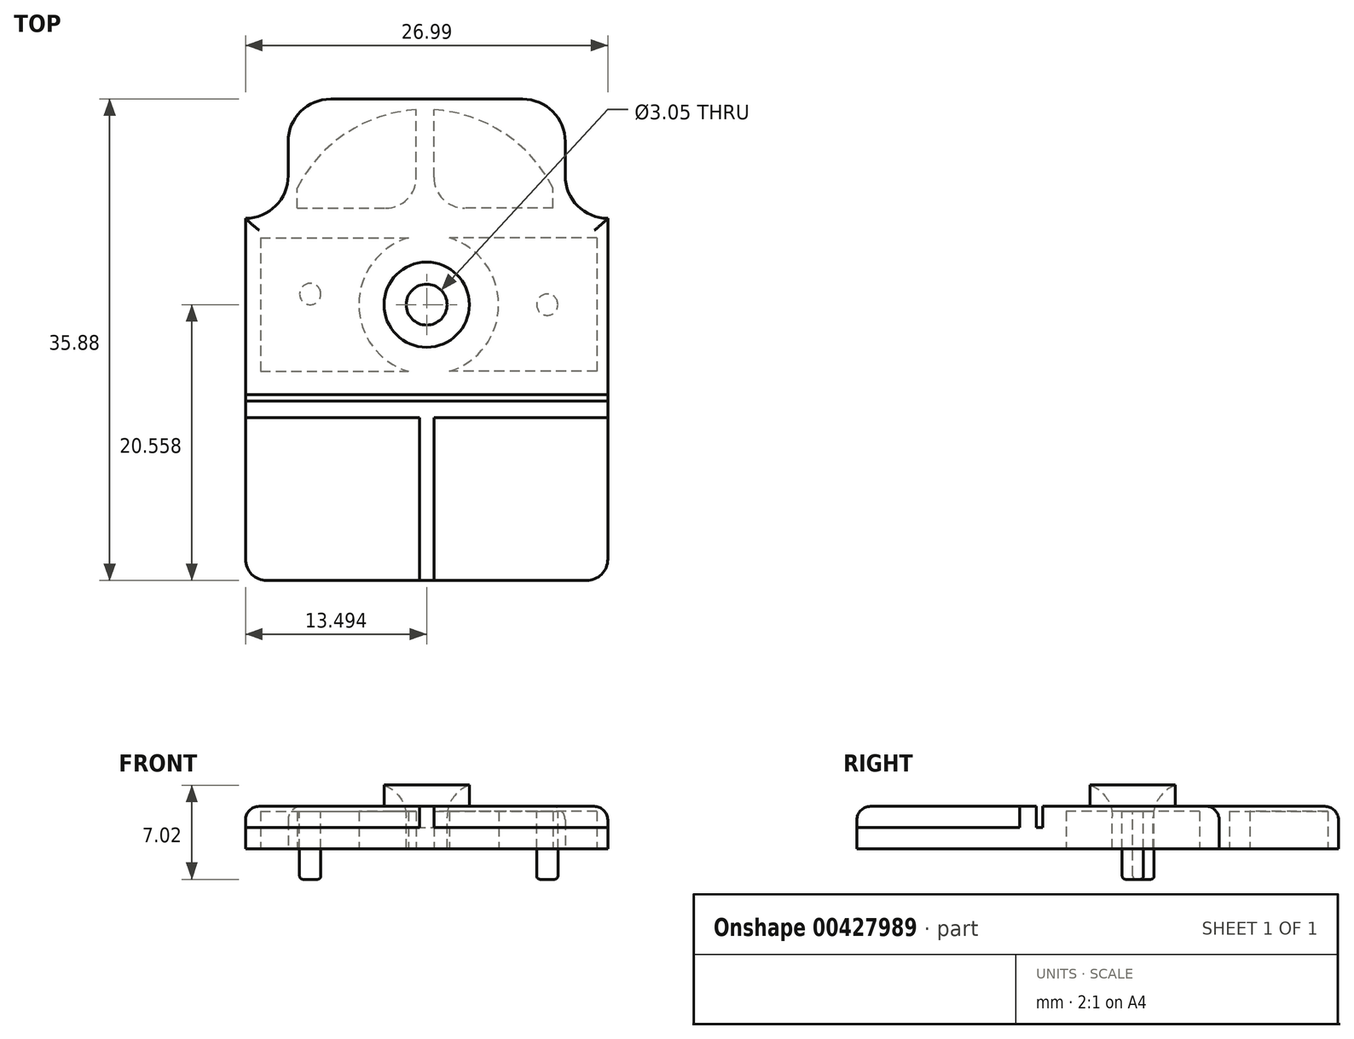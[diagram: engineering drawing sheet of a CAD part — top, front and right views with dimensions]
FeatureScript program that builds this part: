
annotation { "Feature Type Name" : "Feature", "Feature Type Description" : "" }
export const myFeature = defineFeature(function(context is Context, id is Id, definition is map)
    precondition{}
    {
        {
            var Q0;
            Q0=qCreatedBy(makeId("Top.planeOp"),FACE);
            var sketch = newSketch(context, id + "F0", { "sketchPlane" : qUnion([Q0])});
            skLineSegment(sketch, "E0", {"start": v(1.59, 0) * mm, "end": v(25.4, 0) * mm});
            skLineSegment(sketch, "E1", {"start": v(26.99, 1.59) * mm, "end": v(26.99, 26.99) * mm});
            skLineSegment(sketch, "E2", {"start": v(0, 1.59) * mm, "end": v(0, 26.99) * mm});
            skLineSegment(sketch, "E3", {"start": v(26.99, 26.99) * mm, "end": v(26.99, 26.99) * mm});
            skLineSegment(sketch, "E4", {"start": v(0, 26.99) * mm, "end": v(0, 26.99) * mm});
            skLineSegment(sketch, "E5", {"start": v(23.81, 30.16) * mm, "end": v(23.81, 32.7) * mm});
            skLineSegment(sketch, "E6", {"start": v(3.18, 30.16) * mm, "end": v(3.18, 32.7) * mm});
            skLineSegment(sketch, "E7", {"start": v(6.35, 35.88) * mm, "end": v(20.64, 35.88) * mm});
            skPoint(sketch, "E8.visualSharp", {"position": v(26.99, 0) * mm});
            skArc(sketch, "E8.filletArc", {"start": v(25.4, 0) * mm, "mid": v(26.52, 0.46) * mm, "end": v(26.99, 1.59) * mm});
            skPoint(sketch, "E9.visualSharp", {"position": v(0, 0) * mm});
            skArc(sketch, "E9.filletArc", {"start": v(0, 1.59) * mm, "mid": v(0.46, 0.46) * mm, "end": v(1.59, 0) * mm});
            skPoint(sketch, "E10.visualSharp", {"position": v(23.81, 35.88) * mm});
            skArc(sketch, "E10.filletArc", {"start": v(23.81, 32.7) * mm, "mid": v(22.88, 34.95) * mm, "end": v(20.64, 35.88) * mm});
            skPoint(sketch, "E11.visualSharp", {"position": v(3.18, 35.88) * mm});
            skArc(sketch, "E11.filletArc", {"start": v(6.35, 35.88) * mm, "mid": v(4.1, 34.95) * mm, "end": v(3.17, 32.7) * mm});
            skPoint(sketch, "E12.visualSharp", {"position": v(23.81, 26.99) * mm});
            skArc(sketch, "E12.filletArc", {"start": v(23.81, 30.16) * mm, "mid": v(24.74, 27.92) * mm, "end": v(26.99, 26.99) * mm});
            skPoint(sketch, "E13.visualSharp", {"position": v(3.18, 26.99) * mm});
            skArc(sketch, "E13.filletArc", {"start": v(0, 26.99) * mm, "mid": v(2.25, 27.92) * mm, "end": v(3.18, 30.16) * mm});
            skSolve(sketch);
        }
        {
            var Q0;
            Q0=makeQuery(id+"F0.imprint","IMPRINT",FACE,{"disambiguationData":[TD([[makeQuery(id+"F0.imprint","IMPRINT",EDGE,{"derivedFrom":sQuery(id+"F0.wireOp",EDGE,"E0")}),1.0]])]});
            extrude(context, id + "F1", {"entities" : qUnion([Q0]), "depth" : 3.17 * mm});
        }
        {
            var Q0;
            Q0=makeQuery(id+"F1.opExtrude","CAP_EDGE",EDGE,{"disambiguationData":[OSD([sQuery(id+"F0.wireOp",EDGE,"E1")])],"isStart":false});
            var Q1;
            Q1=makeQuery(id+"F1.opExtrude","CAP_EDGE",EDGE,{"disambiguationData":[OSD([sQuery(id+"F0.wireOp",EDGE,"E6")])],"isStart":false});
            fillet(context, id + "F2", {"entities" : qUnion([Q0, Q1]), "radius" : 1.02 * mm, "tangentPropagation" : true, "allowEdgeOverflow" : false});
        }
        {
            var Q0;
            Q0=makeQuery(id+"F1.opExtrude","CAP_FACE",FACE,{"disambiguationData":[OSD([sQuery(id+"F0.wireOp",EDGE,"E0"),sQuery(id+"F0.wireOp",EDGE,"E1"),sQuery(id+"F0.wireOp",EDGE,"E2"),sQuery(id+"F0.wireOp",EDGE,"E5"),sQuery(id+"F0.wireOp",EDGE,"E6"),sQuery(id+"F0.wireOp",EDGE,"E7"),sQuery(id+"F0.wireOp",EDGE,"E8.filletArc"),sQuery(id+"F0.wireOp",EDGE,"E9.filletArc"),sQuery(id+"F0.wireOp",EDGE,"E10.filletArc"),sQuery(id+"F0.wireOp",EDGE,"E11.filletArc"),sQuery(id+"F0.wireOp",EDGE,"E12.filletArc"),sQuery(id+"F0.wireOp",EDGE,"E13.filletArc")])],"isStart":false});
            var sketch = newSketch(context, id + "F3", { "sketchPlane" : qUnion([Q0])});
            skLineSegment(sketch, "E14.bottom", {"start": v(14.03, 12.13) * mm, "end": v(43.3, 12.13) * mm});
            skLineSegment(sketch, "E14.top", {"start": v(14.03, -10.4) * mm, "end": v(43.3, -10.4) * mm});
            skLineSegment(sketch, "E14.left", {"start": v(14.03, 12.13) * mm, "end": v(14.03, -10.4) * mm});
            skLineSegment(sketch, "E14.right", {"start": v(43.3, 12.13) * mm, "end": v(43.3, -10.4) * mm});
            skLineSegment(sketch, "E15.bottom", {"start": v(12.95, 12.13) * mm, "end": v(-5.57, 12.13) * mm});
            skLineSegment(sketch, "E15.top", {"start": v(12.95, -10.91) * mm, "end": v(-5.57, -10.91) * mm});
            skLineSegment(sketch, "E15.left", {"start": v(12.95, 12.13) * mm, "end": v(12.95, -10.91) * mm});
            skLineSegment(sketch, "E15.right", {"start": v(-5.57, 12.13) * mm, "end": v(-5.57, -10.91) * mm});
            skPoint(sketch, "E16.oppositeSnap0", {"position": v(25.97, 13.84) * mm});
            skLineSegment(sketch, "E16.bottom", {"start": v(-5.57, 13.38) * mm, "end": v(34.33, 13.38) * mm});
            skLineSegment(sketch, "E16.top", {"start": v(-5.57, 13.84) * mm, "end": v(34.33, 13.84) * mm});
            skLineSegment(sketch, "E16.left", {"start": v(-5.57, 13.38) * mm, "end": v(-5.57, 13.84) * mm});
            skLineSegment(sketch, "E16.right", {"start": v(34.33, 13.38) * mm, "end": v(34.33, 13.84) * mm});
            skSolve(sketch);
        }
        {
            var Q0;
            {var subQ2=sQuery(id+"F3.wireOp",EDGE,"E14.top");Q0=makeQuery(id+"F3.imprint","IMPRINT",FACE,{"disambiguationData":[TD([[makeQuery(id+"F3.imprint","IMPRINT",EDGE,{"derivedFrom":subQ2}),1.0]])]});}
            var Q1;
            {var subQ0=sQuery(id+"F0.wireOp",EDGE,"E8.filletArc");var subQ1=sQuery(id+"F0.wireOp",EDGE,"E1");var subQ2=sQuery(id+"F0.wireOp",EDGE,"E0");var subQ3=makeQuery(id+"F1.opExtrude","CAP_FACE",FACE,{"disambiguationData":[OSD([subQ2,subQ1,sQuery(id+"F0.wireOp",EDGE,"E2"),sQuery(id+"F0.wireOp",EDGE,"E5"),sQuery(id+"F0.wireOp",EDGE,"E6"),sQuery(id+"F0.wireOp",EDGE,"E7"),subQ0,sQuery(id+"F0.wireOp",EDGE,"E9.filletArc"),sQuery(id+"F0.wireOp",EDGE,"E10.filletArc"),sQuery(id+"F0.wireOp",EDGE,"E11.filletArc"),sQuery(id+"F0.wireOp",EDGE,"E12.filletArc"),sQuery(id+"F0.wireOp",EDGE,"E13.filletArc")])],"isStart":false});var subQ4=makeQuery(id+"F2.opFillet","BLEND_EDGE",EDGE,{"blendedFrom":[makeQuery(id+"F1.opExtrude","CAP_EDGE",EDGE,{"disambiguationData":[OSD([subQ0])],"isStart":false}),subQ3],"blendedInto":[subQ3]});Q1=makeQuery(id+"F3.imprint","IMPRINT",FACE,{"disambiguationData":[TD([[makeQuery(id+"F3.imprint","IMPRINT",EDGE,{"derivedFrom":subQ4}),1.0]])]});}
            var Q2;
            {var subQ0=sQuery(id+"F0.wireOp",EDGE,"E9.filletArc");var subQ1=sQuery(id+"F0.wireOp",EDGE,"E2");var subQ2=sQuery(id+"F0.wireOp",EDGE,"E0");var subQ3=makeQuery(id+"F1.opExtrude","CAP_FACE",FACE,{"disambiguationData":[OSD([subQ2,sQuery(id+"F0.wireOp",EDGE,"E1"),subQ1,sQuery(id+"F0.wireOp",EDGE,"E5"),sQuery(id+"F0.wireOp",EDGE,"E6"),sQuery(id+"F0.wireOp",EDGE,"E7"),sQuery(id+"F0.wireOp",EDGE,"E8.filletArc"),subQ0,sQuery(id+"F0.wireOp",EDGE,"E10.filletArc"),sQuery(id+"F0.wireOp",EDGE,"E11.filletArc"),sQuery(id+"F0.wireOp",EDGE,"E12.filletArc"),sQuery(id+"F0.wireOp",EDGE,"E13.filletArc")])],"isStart":false});var subQ4=makeQuery(id+"F2.opFillet","BLEND_EDGE",EDGE,{"blendedFrom":[makeQuery(id+"F1.opExtrude","CAP_EDGE",EDGE,{"disambiguationData":[OSD([subQ0])],"isStart":false}),subQ3],"blendedInto":[subQ3]});Q2=makeQuery(id+"F3.imprint","IMPRINT",FACE,{"disambiguationData":[TD([[makeQuery(id+"F3.imprint","IMPRINT",EDGE,{"derivedFrom":subQ4}),1.0]])]});}
            var Q3;
            {var subQ9=sQuery(id+"F3.wireOp",EDGE,"E15.top");Q3=makeQuery(id+"F3.imprint","IMPRINT",FACE,{"disambiguationData":[TD([[makeQuery(id+"F3.imprint","IMPRINT",EDGE,{"derivedFrom":subQ9}),-1.0]])]});}
            var Q4;
            {var subQ0=sQuery(id+"F3.wireOp",EDGE,"E16.bottom");var subQ1=sQuery(id+"F0.wireOp",EDGE,"E2");var subQ2=sQuery(id+"F0.wireOp",EDGE,"E1");var subQ3=makeQuery(id+"F1.opExtrude","CAP_FACE",FACE,{"disambiguationData":[OSD([sQuery(id+"F0.wireOp",EDGE,"E0"),subQ2,subQ1,sQuery(id+"F0.wireOp",EDGE,"E5"),sQuery(id+"F0.wireOp",EDGE,"E6"),sQuery(id+"F0.wireOp",EDGE,"E7"),sQuery(id+"F0.wireOp",EDGE,"E8.filletArc"),sQuery(id+"F0.wireOp",EDGE,"E9.filletArc"),sQuery(id+"F0.wireOp",EDGE,"E10.filletArc"),sQuery(id+"F0.wireOp",EDGE,"E11.filletArc"),sQuery(id+"F0.wireOp",EDGE,"E12.filletArc"),sQuery(id+"F0.wireOp",EDGE,"E13.filletArc")])],"isStart":false});var subQ4=makeQuery(id+"F2.opFillet","BLEND_EDGE",EDGE,{"blendedFrom":[makeQuery(id+"F1.opExtrude","CAP_EDGE",EDGE,{"disambiguationData":[OSD([subQ1])],"isStart":false}),subQ3],"blendedInto":[subQ3]});var subQ5=makeQuery(id+"F3.imprint","INTERSECT",VERTEX,{"derivedFrom":[subQ4,subQ0]});Q4=makeQuery(id+"F3.imprint","IMPRINT",FACE,{"disambiguationData":[TD([[makeQuery(id+"F3.imprint","IMPRINT",EDGE,{"disambiguationData":[TD([[subQ5,-1.0]])],"derivedFrom":subQ0}),1.0]])]});}
            var Q5;
            {var subQ0=sQuery(id+"F3.wireOp",EDGE,"E16.right");Q5=makeQuery(id+"F3.imprint","IMPRINT",FACE,{"disambiguationData":[TD([[makeQuery(id+"F3.imprint","IMPRINT",EDGE,{"derivedFrom":subQ0}),1.0]])]});}
            var Q6;
            {var subQ0=sQuery(id+"F3.wireOp",EDGE,"E16.left");Q6=makeQuery(id+"F3.imprint","IMPRINT",FACE,{"disambiguationData":[TD([[makeQuery(id+"F3.imprint","IMPRINT",EDGE,{"derivedFrom":subQ0}),-1.0]])]});}
            extrude(context, id + "F4", {"entities" : qUnion([Q0, Q1, Q2, Q3, Q4, Q5, Q6]), "operationType" : NewBodyOperationType.REMOVE, "oppositeDirection" : true, "depth" : 1.59 * mm});
        }
        {
            var Q0;
            {var subQ0=sQuery(id+"F0.wireOp",EDGE,"E6");var subQ1=sQuery(id+"F0.wireOp",EDGE,"E5");var subQ2=sQuery(id+"F0.wireOp",EDGE,"E2");var subQ3=sQuery(id+"F0.wireOp",EDGE,"E1");var subQ4=sQuery(id+"F0.wireOp",EDGE,"E7");var subQ5=sQuery(id+"F0.wireOp",EDGE,"E10.filletArc");var subQ6=sQuery(id+"F0.wireOp",EDGE,"E11.filletArc");var subQ7=sQuery(id+"F0.wireOp",EDGE,"E12.filletArc");var subQ8=sQuery(id+"F0.wireOp",EDGE,"E13.filletArc");Q0=makeQuery(id+"F4.boolean.opBoolean","SPLIT",FACE,{"disambiguationData":[TD([makeQuery(id+"F2.opFillet","BLEND_FACE",FACE,{"disambiguationData":[OSD([subQ1])]})])],"derivedFrom":makeQuery(id+"F1.opExtrude","CAP_FACE",FACE,{"disambiguationData":[OSD([sQuery(id+"F0.wireOp",EDGE,"E0"),subQ3,subQ2,subQ1,subQ0,subQ4,sQuery(id+"F0.wireOp",EDGE,"E8.filletArc"),sQuery(id+"F0.wireOp",EDGE,"E9.filletArc"),subQ5,subQ6,subQ7,subQ8])],"isStart":false})});}
            var sketch = newSketch(context, id + "F5", { "sketchPlane" : qUnion([Q0])});
            skCircle(sketch, "E17", {"center": v(13.5, 20.56) * mm, "radius": 1.52 * mm});
            skPoint(sketch, "E17.centerSnap0", {"position": v(13.5, 34.86) * mm});
            skCircle(sketch, "E18", {"center": v(13.5, 20.56) * mm, "radius": 3.18 * mm});
            skSolve(sketch);
        }
        {
            var Q0;
            Q0=makeQuery(id+"F5.imprint","IMPRINT",FACE,{"disambiguationData":[TD([[makeQuery(id+"F5.imprint","IMPRINT",EDGE,{"derivedFrom":sQuery(id+"F5.wireOp",EDGE,"E17")}),1.0]])]});
            extrude(context, id + "F6", {"entities" : qUnion([Q0]), "operationType" : NewBodyOperationType.REMOVE, "oppositeDirection" : true, "depth" : 25.4 * mm});
        }
        {
            var Q0;
            Q0 = qSketchRegion(id + "F5", true);
            extrude(context, id + "F7", {"entities" : qUnion([Q0]), "operationType" : NewBodyOperationType.ADD, "depth" : 1.59 * mm});
        }
        {
            var Q0;
            Q0=makeQuery(id+"F7.opExtrude","CAP_EDGE",EDGE,{"disambiguationData":[OSD([sQuery(id+"F5.wireOp",EDGE,"E17")])],"isStart":false});
            fillet(context, id + "F8", {"entities" : qUnion([Q0]), "radius" : 2.54 * mm, "tangentPropagation" : true, "allowEdgeOverflow" : false});
        }
        {
            var Q0;
            Q0=makeQuery(id+"F1.opExtrude","CAP_FACE",FACE,{"disambiguationData":[OSD([sQuery(id+"F0.wireOp",EDGE,"E0"),sQuery(id+"F0.wireOp",EDGE,"E1"),sQuery(id+"F0.wireOp",EDGE,"E2"),sQuery(id+"F0.wireOp",EDGE,"E5"),sQuery(id+"F0.wireOp",EDGE,"E6"),sQuery(id+"F0.wireOp",EDGE,"E7"),sQuery(id+"F0.wireOp",EDGE,"E8.filletArc"),sQuery(id+"F0.wireOp",EDGE,"E9.filletArc"),sQuery(id+"F0.wireOp",EDGE,"E10.filletArc"),sQuery(id+"F0.wireOp",EDGE,"E11.filletArc"),sQuery(id+"F0.wireOp",EDGE,"E12.filletArc"),sQuery(id+"F0.wireOp",EDGE,"E13.filletArc")])],"isStart":true});
            var sketch = newSketch(context, id + "F9", { "sketchPlane" : qUnion([Q0])});
            skLineSegment(sketch, "E19", {"start": v(13.5, -20.56) * mm, "end": v(26.18, -20.56) * mm});
            skLineSegment(sketch, "E20", {"start": v(26.18, -20.56) * mm, "end": v(26.18, -15.58) * mm});
            skLineSegment(sketch, "E21", {"start": v(26.18, -15.58) * mm, "end": v(15.18, -15.58) * mm});
            skLineSegment(sketch, "E22.MirrorCS", {"start": v(26.18, -25.54) * mm, "end": v(15.18, -25.54) * mm});
            skLineSegment(sketch, "E23.MirrorCS", {"start": v(26.18, -20.56) * mm, "end": v(26.18, -25.54) * mm});
            skArc(sketch, "E24", {"start": v(15.18, -25.54) * mm, "mid": v(18.86, -20.56) * mm, "end": v(15.18, -15.58) * mm});
            skLineSegment(sketch, "E25", {"start": v(13.65, -20.56) * mm, "end": v(13.65, -10.86) * mm});
            skLineSegment(sketch, "E26", {"start": v(24.89, -25.54) * mm, "end": v(24.89, -24.05) * mm});
            skLineSegment(sketch, "E27", {"start": v(24.89, -24.05) * mm, "end": v(26.18, -24.05) * mm});
            skLineSegment(sketch, "E28.MirrorCS", {"start": v(1.12, -15.58) * mm, "end": v(12.13, -15.58) * mm});
            skArc(sketch, "E29.MirrorCS", {"start": v(12.13, -25.54) * mm, "mid": v(8.44, -20.56) * mm, "end": v(12.13, -15.58) * mm});
            skLineSegment(sketch, "E30.MirrorCS", {"start": v(1.12, -20.56) * mm, "end": v(1.12, -15.58) * mm});
            skLineSegment(sketch, "E31.MirrorCS", {"start": v(1.12, -20.56) * mm, "end": v(1.12, -25.54) * mm});
            skLineSegment(sketch, "E32.MirrorCS", {"start": v(1.12, -25.54) * mm, "end": v(12.13, -25.54) * mm});
            skSolve(sketch);
        }
        {
            var Q0;
            Q0 = qSketchRegion(id + "F9", true);
            extrude(context, id + "F10", {"entities" : qUnion([Q0]), "operationType" : NewBodyOperationType.REMOVE, "oppositeDirection" : true, "depth" : 2.82 * mm});
        }
        {
            var Q0;
            Q0=makeQuery(id+"F10.boolean.opBoolean","COPY",FACE,{"derivedFrom":makeQuery(id+"F10.opExtrude","CAP_FACE",FACE,{"disambiguationData":[OSD([sQuery(id+"F9.wireOp",EDGE,"E20"),sQuery(id+"F9.wireOp",EDGE,"E21"),sQuery(id+"F9.wireOp",EDGE,"E22.MirrorCS"),sQuery(id+"F9.wireOp",EDGE,"E23.MirrorCS"),sQuery(id+"F9.wireOp",EDGE,"E24")])],"isStart":false})});
            var sketch = newSketch(context, id + "F11", { "sketchPlane" : qUnion([Q0])});
            skCircle(sketch, "E33", {"center": v(22.48, -20.56) * mm, "radius": 0.8 * mm});
            skPoint(sketch, "E33.centerSnap0", {"position": v(18.86, -20.56) * mm});
            skCircle(sketch, "E34.MirrorC", {"center": v(4.82, -21.35) * mm, "radius": 0.8 * mm});
            skSolve(sketch);
        }
        {
            var Q0;
            Q0 = qSketchRegion(id + "F11", true);
            extrude(context, id + "F12", {"entities" : qUnion([Q0]), "operationType" : NewBodyOperationType.ADD, "depth" : 5.08 * mm});
        }
        {
            var Q0;
            Q0=makeQuery(id+"F12.opExtrude","CAP_EDGE",EDGE,{"disambiguationData":[OSD([sQuery(id+"F11.wireOp",EDGE,"E33")])],"isStart":false});
            var Q1;
            Q1=makeQuery(id+"F12.opExtrude","CAP_EDGE",EDGE,{"disambiguationData":[OSD([sQuery(id+"F11.wireOp",EDGE,"E34.MirrorC")])],"isStart":false});
            fillet(context, id + "F13", {"entities" : qUnion([Q0, Q1]), "radius" : 0.25 * mm, "tangentPropagation" : true, "allowEdgeOverflow" : false});
        }
        {
            var Q0;
            Q0=makeQuery(id+"F1.opExtrude","CAP_FACE",FACE,{"disambiguationData":[OSD([sQuery(id+"F0.wireOp",EDGE,"E0"),sQuery(id+"F0.wireOp",EDGE,"E1"),sQuery(id+"F0.wireOp",EDGE,"E2"),sQuery(id+"F0.wireOp",EDGE,"E5"),sQuery(id+"F0.wireOp",EDGE,"E6"),sQuery(id+"F0.wireOp",EDGE,"E7"),sQuery(id+"F0.wireOp",EDGE,"E8.filletArc"),sQuery(id+"F0.wireOp",EDGE,"E9.filletArc"),sQuery(id+"F0.wireOp",EDGE,"E10.filletArc"),sQuery(id+"F0.wireOp",EDGE,"E11.filletArc"),sQuery(id+"F0.wireOp",EDGE,"E12.filletArc"),sQuery(id+"F0.wireOp",EDGE,"E13.filletArc")])],"isStart":true});
            var sketch = newSketch(context, id + "F14", { "sketchPlane" : qUnion([Q0])});
            skLineSegment(sketch, "E35", {"start": v(3.85, -27.75) * mm, "end": v(3.85, -29.26) * mm});
            skLineSegment(sketch, "E36", {"start": v(3.85, -27.75) * mm, "end": v(10.44, -27.75) * mm});
            skLineSegment(sketch, "E37", {"start": v(12.72, -30.04) * mm, "end": v(12.72, -35.08) * mm});
            skArc(sketch, "E38", {"start": v(3.85, -29.26) * mm, "mid": v(7.51, -33.35) * mm, "end": v(12.72, -35.08) * mm});
            skPoint(sketch, "E39.visualSharp", {"position": v(12.72, -27.75) * mm});
            skArc(sketch, "E39.filletArc", {"start": v(12.72, -30.04) * mm, "mid": v(12.05, -28.42) * mm, "end": v(10.44, -27.75) * mm});
            skArc(sketch, "E40.MirrorCS", {"start": v(22.9, -29.26) * mm, "mid": v(19.25, -33.35) * mm, "end": v(14.04, -35.08) * mm});
            skLineSegment(sketch, "E41.MirrorCS", {"start": v(14.04, -30.04) * mm, "end": v(14.04, -35.08) * mm});
            skArc(sketch, "E42.MirrorCS", {"start": v(14.04, -30.04) * mm, "mid": v(14.7, -28.42) * mm, "end": v(16.32, -27.75) * mm});
            skLineSegment(sketch, "E43.MirrorCS", {"start": v(22.9, -27.75) * mm, "end": v(16.32, -27.75) * mm});
            skLineSegment(sketch, "E44.MirrorCS", {"start": v(22.9, -27.75) * mm, "end": v(22.9, -29.26) * mm});
            skSolve(sketch);
        }
        {
            var Q0;
            Q0 = qSketchRegion(id + "F14", true);
            extrude(context, id + "F15", {"entities" : qUnion([Q0]), "operationType" : NewBodyOperationType.REMOVE, "oppositeDirection" : true, "depth" : 2.82 * mm});
        }
    });
